# Revit family: BM-00483_TET1UA
name_source: partatom
category: Generic Models
revit_build: Autodesk Revit LT 2016 (Build: 20151007_0715(x64)
units: mm (PartAtom-declared; Revit-internal decimal feet)

## family parameters
Always vertical = Yes
Can host rebar = No
Cut with Voids When Loaded = No
Part Type = Normal
Room Calculation Point = No
Round Connector Dimension = Use Diameter
Shared = No
Work Plane-Based = No

## types (1)
- BM-00483_TET1UA
    Codes/Standards = •Meets or exceeds 1037/ASME A112.1037/CSA B125.37
•Certifications: IAPMO(cUPC), EPA WaterSense, ASSE, State of MAssachusetts, and others
•Code Compliance: UPC, IPC, NSPC, NPC Canada, and others
•Complies with CA Title 20 regulations and CalGreen
•ADA compliant
    Colors/Finishes = #CP Polished Chrome
    Manufacturer = TOTO USA
    Model = TET1UA32#CP
    Specifications = • Material Bronze casting
• Power supply EcoPower
• Sensor detection time Factory setting at six
(6) seconds minimum
• Sensor detection range Self-adjusting to
environment
• Discharge quantity Preset to 1.28 gpf/
4.8 lpf
• Operating temperature 32°-104°F (0°-40°C)
• Water supply pressure 35 psi - 125 psi*
• Water supply connection 1" NPT
• Warranty Three year limited
    h = 0' - 11 1/8"
    material = Steel, Galvanized

## geometry (parser evidence)
native form markers: Sweep x2
no freeform markers — native parametric forms only
